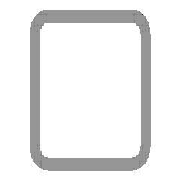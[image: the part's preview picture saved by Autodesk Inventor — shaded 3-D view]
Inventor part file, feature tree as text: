
AUTODESK INVENTOR PART (.ipt)
format: ipt  version: 2025.1 (Build 291241020, 241B)  size: 145,408 bytes
history: native  units: mm (DEFAULTED — no unit token found)
features: other x4, sketch x1, plane x1
ambient origin geometry x8: Origin, YZ Plane, XZ Plane, XY Plane, X Axis, Y Axis, Z Axis, Center Point
bodies: Solid1 (feature_tree), Body (feature_tree)
feature tree (6):
  parser-record x1  (decoder bookkeeping rows leaked as tree rows — omitted from the tree; the rows remain in map.json)
  other  "Driven Length"
  other  "Start plane"
  other  "End plane"
  sketch  "Sketch3"  dims[d3=950.0mm d4=0.0mm d7=6.0mm d9=100.0mm d11=100.0mm d12=3.0mm d13=50.0mm d14=1000.0mm d15=50.0mm d16=50.0mm d17=90.0deg d18=950.0mm]
  plane  "Work Plane3"
